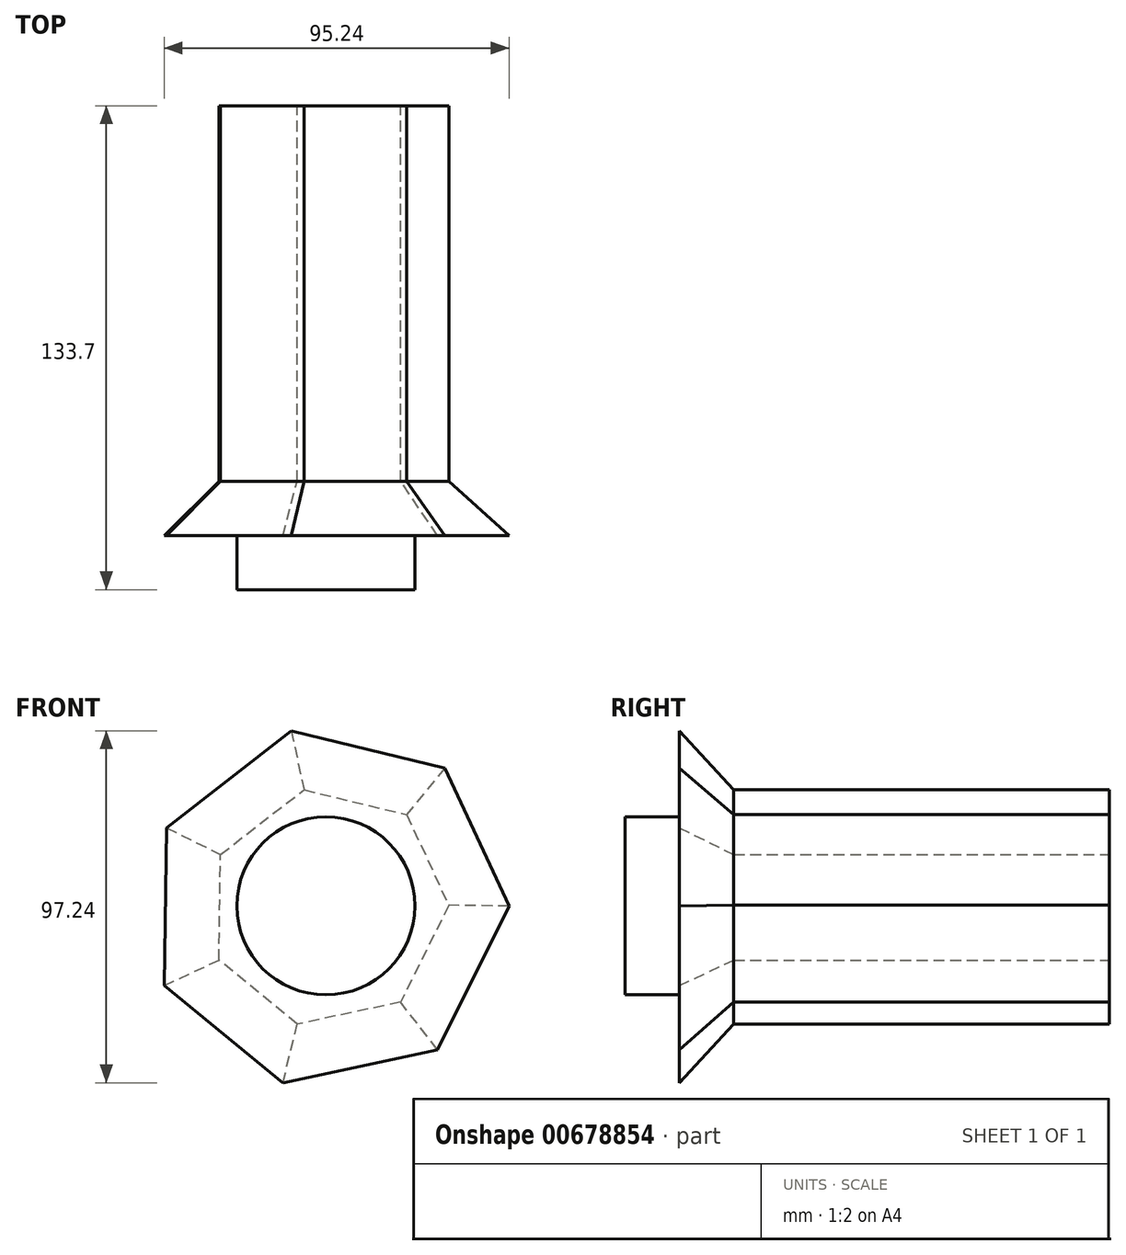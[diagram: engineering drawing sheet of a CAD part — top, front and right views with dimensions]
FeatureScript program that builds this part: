
annotation { "Feature Type Name" : "Feature", "Feature Type Description" : "" }
export const myFeature = defineFeature(function(context is Context, id is Id, definition is map)
    precondition{}
    {
        {
            var Q0;
            Q0=qCreatedBy(makeId("Front.planeOp"),FACE);
            var sketch = newSketch(context, id + "F0", { "sketchPlane" : qUnion([Q0])});
            skLineSegment(sketch, "E0.0", {"start": v(-6.06, 32.08) * mm, "end": v(22.32, 25.2) * mm});
            skLineSegment(sketch, "E0.1", {"start": v(22.32, 25.2) * mm, "end": v(33.96, 0.16) * mm});
            skLineSegment(sketch, "E0.2", {"start": v(33.96, 0.16) * mm, "end": v(20.62, -26.6) * mm});
            skLineSegment(sketch, "E0.3", {"start": v(20.62, -26.6) * mm, "end": v(-7.93, -32.7) * mm});
            skLineSegment(sketch, "E0.4", {"start": v(-7.93, -32.7) * mm, "end": v(-29.53, -15) * mm});
            skLineSegment(sketch, "E0.5", {"start": v(-29.53, -15) * mm, "end": v(-29.14, 14.18) * mm});
            skLineSegment(sketch, "E0.6", {"start": v(-29.14, 14.18) * mm, "end": v(-6.06, 32.08) * mm});
            skSolve(sketch);
        }
        {
            var Q0;
            Q0=makeQuery(id+"F0.imprint","IMPRINT",FACE,{"disambiguationData":[TD([[makeQuery(id+"F0.imprint","IMPRINT",EDGE,{"derivedFrom":sQuery(id+"F0.wireOp",EDGE,"E0.0")}),-1.0]])]});
            extrude(context, id + "F1", {"entities" : qUnion([Q0]), "depth" : 103.7 * mm, "offsetDistance" : 25 * mm});
        }
        {
            var Q0;
            Q0=makeQuery(id+"F1.opExtrude","CAP_FACE",FACE,{"disambiguationData":[OSD([sQuery(id+"F0.wireOp",EDGE,"E0.0"),sQuery(id+"F0.wireOp",EDGE,"E0.1"),sQuery(id+"F0.wireOp",EDGE,"E0.2"),sQuery(id+"F0.wireOp",EDGE,"E0.3"),sQuery(id+"F0.wireOp",EDGE,"E0.4"),sQuery(id+"F0.wireOp",EDGE,"E0.5"),sQuery(id+"F0.wireOp",EDGE,"E0.6")])],"isStart":false});
            var sketch = newSketch(context, id + "F2", { "sketchPlane" : qUnion([Q0])});
            skCircle(sketch, "E1", {"center": v(0, 0) * mm, "radius": 24.6 * mm});
            skSolve(sketch);
        }
        {
            var Q0;
            Q0 = qSketchRegion(id + "F2", true);
            extrude(context, id + "F3", {"entities" : qUnion([Q0]), "operationType" : NewBodyOperationType.ADD, "surfaceOperationType" : NewSurfaceOperationType.ADD, "depth" : 30 * mm, "offsetDistance" : 25 * mm});
        }
        {
            var Q0;
            Q0=makeQuery(id+"F1.opExtrude","CAP_FACE",FACE,{"disambiguationData":[OSD([sQuery(id+"F0.wireOp",EDGE,"E0.0"),sQuery(id+"F0.wireOp",EDGE,"E0.1"),sQuery(id+"F0.wireOp",EDGE,"E0.2"),sQuery(id+"F0.wireOp",EDGE,"E0.3"),sQuery(id+"F0.wireOp",EDGE,"E0.4"),sQuery(id+"F0.wireOp",EDGE,"E0.5"),sQuery(id+"F0.wireOp",EDGE,"E0.6")])],"isStart":false});
            extrude(context, id + "F4", {"entities" : qUnion([Q0]), "operationType" : NewBodyOperationType.ADD, "depth" : 15 * mm, "offsetDistance" : 25 * mm, "hasDraft" : true, "draftAngle" : 45 * degree});
        }
    });
